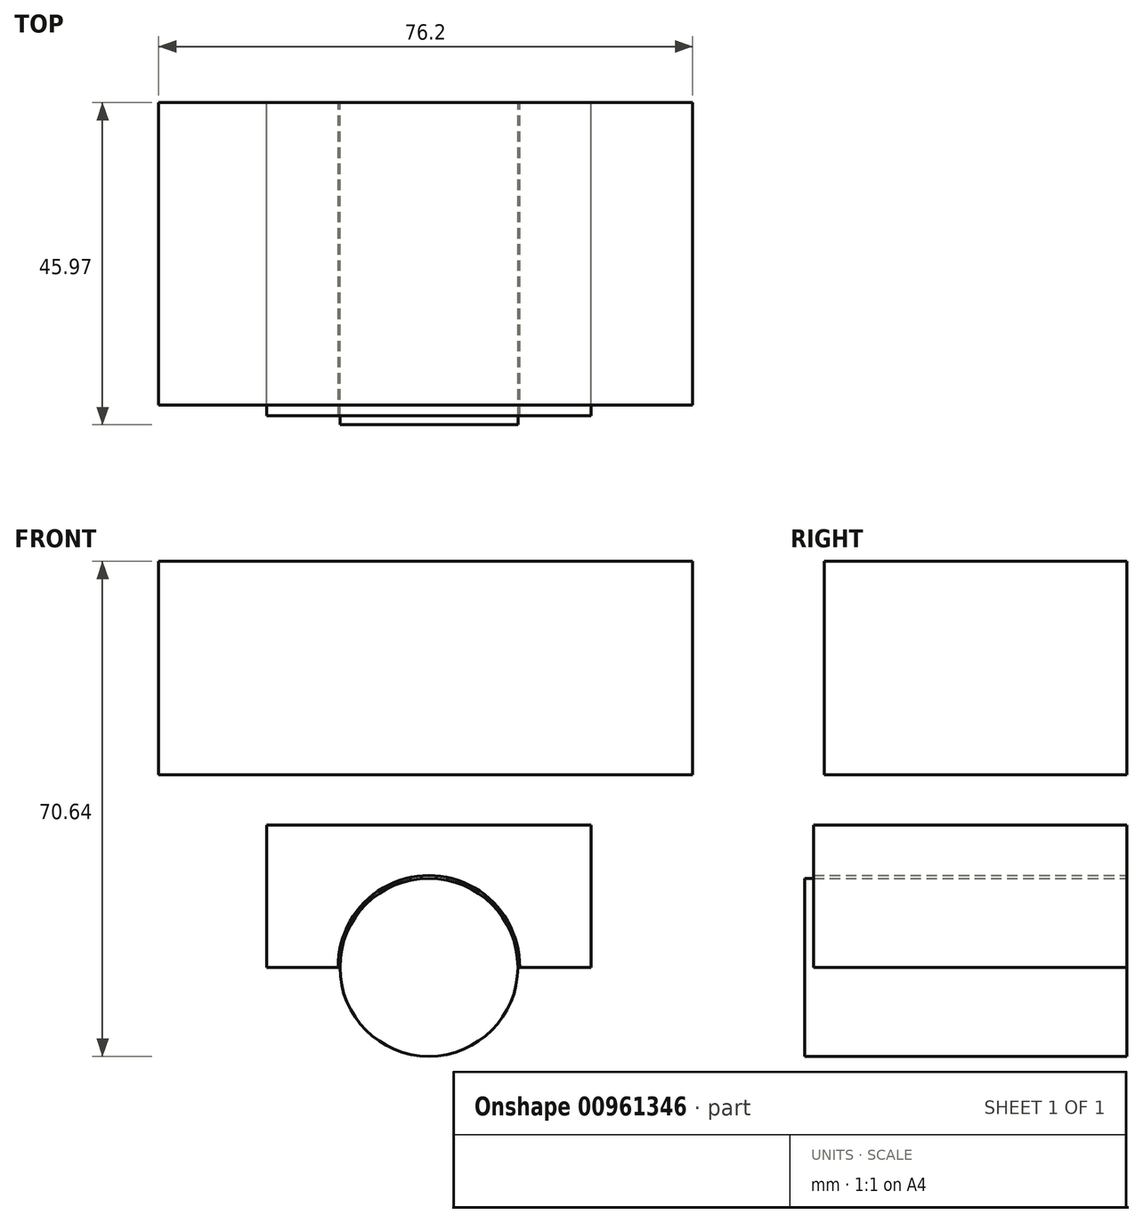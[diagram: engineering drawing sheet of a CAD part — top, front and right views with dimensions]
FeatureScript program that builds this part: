
annotation { "Feature Type Name" : "Feature", "Feature Type Description" : "" }
export const myFeature = defineFeature(function(context is Context, id is Id, definition is map)
    precondition{}
    {
        {
            var Q0;
            Q0=qCreatedBy(makeId("Front.planeOp"),FACE);
            var sketch = newSketch(context, id + "F0", { "sketchPlane" : qUnion([Q0])});
            skCircle(sketch, "E0", {"center": v(0, 0) * mm, "radius": 12.7 * mm});
            skSolve(sketch);
        }
        {
            var Q0;
            Q0=makeQuery(id+"F0.imprint","IMPRINT",FACE,{"disambiguationData":[TD([[makeQuery(id+"F0.imprint","IMPRINT",EDGE,{"derivedFrom":sQuery(id+"F0.wireOp",EDGE,"E0")}),1.0]])]});
            var Q1;
            Q1=sQuery(id+"F0.wireOp",EDGE,"E0");
            extrude(context, id + "F1", {"entities" : qUnion([Q0]), "surfaceEntities" : qUnion([Q1]), "depth" : 45.97 * mm, "offsetDistance" : 25.4 * mm});
        }
        {
            var Q0;
            Q0=qCreatedBy(makeId("Front.planeOp"),FACE);
            var sketch = newSketch(context, id + "F2", { "sketchPlane" : qUnion([Q0])});
            skPoint(sketch, "E1", {"position": v(-12.95, 0) * mm});
            skPoint(sketch, "E2", {"position": v(12.95, 0) * mm});
            skArc(sketch, "E3", {"start": v(12.95, 0) * mm, "mid": v(0, 13.09) * mm, "end": v(-12.95, 0) * mm});
            skLineSegment(sketch, "E4", {"start": v(-12.95, 0) * mm, "end": v(-23.11, 0) * mm});
            skLineSegment(sketch, "E5", {"start": v(-23.11, 0) * mm, "end": v(-23.11, 20.32) * mm});
            skLineSegment(sketch, "E6", {"start": v(-23.11, 20.32) * mm, "end": v(23.11, 20.32) * mm});
            skLineSegment(sketch, "E7", {"start": v(23.11, 20.32) * mm, "end": v(23.11, 0) * mm});
            skLineSegment(sketch, "E8", {"start": v(23.11, 0) * mm, "end": v(12.95, 0) * mm});
            skSolve(sketch);
        }
        {
            var Q0;
            Q0=makeQuery(id+"F2.imprint","IMPRINT",FACE,{"disambiguationData":[TD([[makeQuery(id+"F2.imprint","IMPRINT",EDGE,{"derivedFrom":sQuery(id+"F2.wireOp",EDGE,"E3")}),-1.0]])]});
            extrude(context, id + "F3", {"entities" : qUnion([Q0]), "depth" : 44.7 * mm, "offsetDistance" : 25.4 * mm});
        }
        {
            var Q0;
            Q0=qCreatedBy(makeId("Front.planeOp"),FACE);
            var sketch = newSketch(context, id + "F4", { "sketchPlane" : qUnion([Q0])});
            skLineSegment(sketch, "E9.bottom", {"start": v(-38.56, 57.94) * mm, "end": v(37.64, 57.94) * mm});
            skLineSegment(sketch, "E9.top", {"start": v(-38.56, 27.46) * mm, "end": v(37.64, 27.46) * mm});
            skLineSegment(sketch, "E9.left", {"start": v(-38.56, 57.94) * mm, "end": v(-38.56, 27.46) * mm});
            skLineSegment(sketch, "E9.right", {"start": v(37.64, 57.94) * mm, "end": v(37.64, 27.46) * mm});
            skSolve(sketch);
        }
        {
            var Q0;
            Q0=makeQuery(id+"F4.imprint","IMPRINT",FACE,{"disambiguationData":[TD([[makeQuery(id+"F4.imprint","IMPRINT",EDGE,{"derivedFrom":sQuery(id+"F4.wireOp",EDGE,"E9.bottom")}),-1.0]])]});
            extrude(context, id + "F5", {"entities" : qUnion([Q0]), "depth" : 43.18 * mm, "offsetDistance" : 25.4 * mm});
        }
        {
            var Q0;
            Q0=makeQuery(id+"F1.opExtrude","SWEPT_BODY",BODY,{"disambiguationData":[OSD([sQuery(id+"F0.wireOp",EDGE,"E0")])]});
            var Q1;
            Q1=makeQuery(id+"F3.opExtrude","SWEPT_BODY",BODY,{"disambiguationData":[OSD([sQuery(id+"F2.wireOp",EDGE,"E3"),sQuery(id+"F2.wireOp",EDGE,"E4"),sQuery(id+"F2.wireOp",EDGE,"E5"),sQuery(id+"F2.wireOp",EDGE,"E6"),sQuery(id+"F2.wireOp",EDGE,"E7"),sQuery(id+"F2.wireOp",EDGE,"E8")])]});
            var Q2;
            Q2=makeQuery(id+"F5.opExtrude","SWEPT_BODY",BODY,{"disambiguationData":[OSD([sQuery(id+"F4.wireOp",EDGE,"E9.bottom"),sQuery(id+"F4.wireOp",EDGE,"E9.top"),sQuery(id+"F4.wireOp",EDGE,"E9.left"),sQuery(id+"F4.wireOp",EDGE,"E9.right")])]});
            booleanBodies(context, id + "F6", {"operationType" : BooleanOperationType.SUBTRACTION, "tools" : qUnion([Q0, Q1]), "targets" : qUnion([Q2]), "keepTools" : true});
        }
    });
